# Revit family: Anschlussadapter für Rohrschellen
name_source: partatom
category: HLS-Bauteile
revit_build: Autodesk Revit 2017 (Build: 20190507_1515(x64)
units: mm (PartAtom-declared; Revit-internal decimal feet)

## family parameters
Arbeitsebenenbasiert = Ja
Beim Laden mit Abzugskörper schneiden = Nein
Bemaßung runder Anschluss = Durchmesser verwenden
Gemeinsam genutzt = Ja
Immer vertikal = Nein
Raumberechnungspunkt = Nein
Teiletyp = Normal

## types (3) — shared parameters
D = 25 mm  [stored 0.082021 ft]
D0 = 20 mm  [stored 0.0656168 ft]
Fabrikat = MEFA
Firma = MEFA Befestigungs- und Montagesysteme GmbH
Kurztext1 = Anschlussadapter rund
L2 = 15 mm  [stored 0.0492126 ft]
Material = Stahl
Mengeneinheit = St
Oberflaeche = galvanisch verzinkt
Vorgabe-Ansicht = 1219 mm
vpe = 1 St

## per-type parameters (varying)
| type | Artikelnummer | EAN | Gewicht | Gewicht pro Bauteil | Kurztext2 | L1 | LG | Länge | d1 |
| Für Trabant und Omnia mit Anschluss M8/M10 (Muffe1/2") | 0830209 | 4250928420862 | 0.08 kg | 0.08 kg | Innengew. 1/2'' auf Anschluss M8/M10 | 15 mm  [stored 0.0492126 ft] | 31 mm  [stored 0.101706 ft] | 36 mm  [stored 0.11811 ft] | 13 mm |
| Für Maxima PSM, Omnia MB Ø132-168 und Trabant Ø121-168 (Muffe1/2") | 0830204 | 4250928420855 | 0.09 kg | 0.09 kg | Innengew. 1/2'' auf Anschluss M10/M12 | 21 mm  [stored 0.0688976 ft] | 37 mm  [stored 0.121391 ft] | 42 mm  [stored 0.137795 ft] | 13 mm |
| Für Maxima PSM, Omnia MB Ø132-168 und Trabant Ø121-168 (M16) | 0830202 | 4250928420848 | 0.10 kg | 0.10 kg | Innengew. M16 auf Anschluss M10/M12 | 21 mm  [stored 0.0688976 ft] | 37 mm  [stored 0.121391 ft] | 42 mm  [stored 0.137795 ft] | 14 mm  [stored 0.0459318 ft] |

note: [stored X ft] marks values corroborated as IEEE doubles in the binary element streams (Revit-internal decimal feet)
